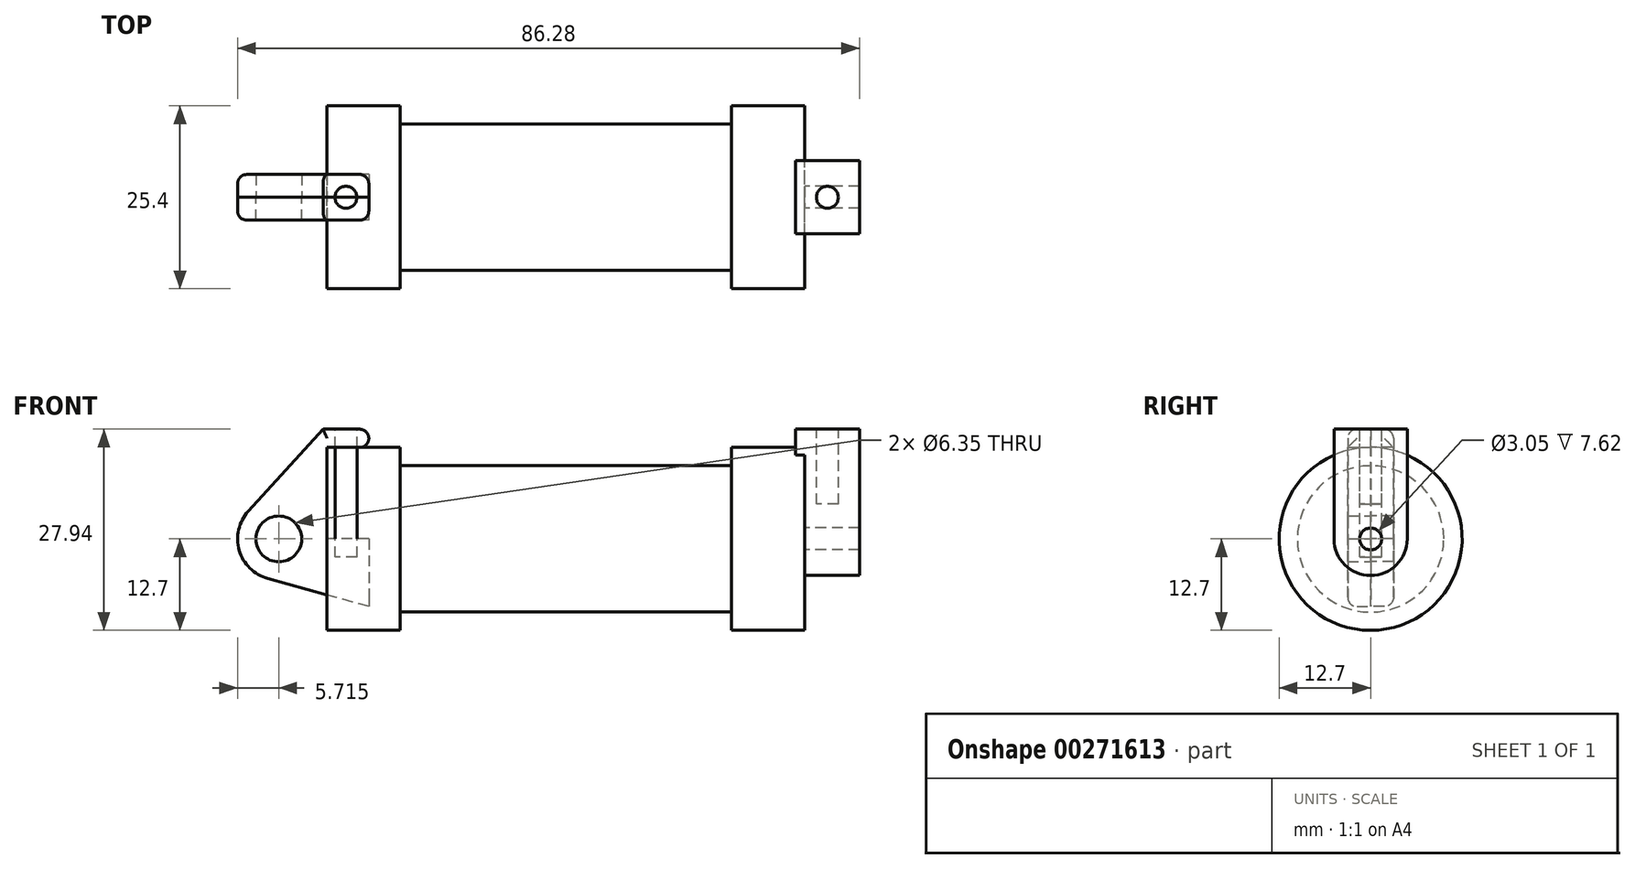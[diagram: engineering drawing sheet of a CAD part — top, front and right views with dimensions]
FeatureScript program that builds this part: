
annotation { "Feature Type Name" : "Feature", "Feature Type Description" : "" }
export const myFeature = defineFeature(function(context is Context, id is Id, definition is map)
    precondition{}
    {
        {
            var Q0;
            Q0=qCreatedBy(makeId("Front.planeOp"),FACE);
            var sketch = newSketch(context, id + "F0", { "sketchPlane" : qUnion([Q0])});
            skLineSegment(sketch, "E0", {"start": v(0, 0) * mm, "end": v(0, 12.7) * mm});
            skLineSegment(sketch, "E1", {"start": v(0, 12.7) * mm, "end": v(10.16, 12.7) * mm});
            skLineSegment(sketch, "E2", {"start": v(10.16, 12.7) * mm, "end": v(10.16, 10.16) * mm});
            skLineSegment(sketch, "E3", {"start": v(10.16, 10.16) * mm, "end": v(56.13, 10.16) * mm});
            skLineSegment(sketch, "E4", {"start": v(56.13, 10.16) * mm, "end": v(56.13, 12.7) * mm});
            skLineSegment(sketch, "E5", {"start": v(56.13, 12.7) * mm, "end": v(66.3, 12.7) * mm});
            skLineSegment(sketch, "E6", {"start": v(66.3, 12.7) * mm, "end": v(66.3, 0) * mm});
            skLineSegment(sketch, "E7", {"start": v(66.3, 0) * mm, "end": v(0, 0) * mm});
            skLineSegment(sketch, "E8", {"start": v(5.84, 15.24) * mm, "end": v(-0.5, 15.24) * mm});
            skLineSegment(sketch, "E9", {"start": v(-0.5, 15.24) * mm, "end": v(-10.88, 3.85) * mm});
            skLineSegment(sketch, "E10", {"start": v(0, 0) * mm, "end": v(-6.65, 0) * mm});
            skCircle(sketch, "E11", {"center": v(-6.65, 0) * mm, "radius": 5.72 * mm});
            skCircle(sketch, "E12", {"center": v(-6.65, 0) * mm, "radius": 3.18 * mm});
            skLineSegment(sketch, "E13", {"start": v(5.84, 15.24) * mm, "end": v(5.84, -9.4) * mm});
            skLineSegment(sketch, "E14", {"start": v(5.84, -9.4) * mm, "end": v(-8.18, -5.5) * mm});
            skSolve(sketch);
        }
        {
            var Q0;
            {var subQ0=sQuery(id+"F0.wireOp",EDGE,"E2");Q0=makeQuery(id+"F0.imprint","IMPRINT",FACE,{"disambiguationData":[TD([[makeQuery(id+"F0.imprint","IMPRINT",EDGE,{"derivedFrom":subQ0}),-1.0]])]});}
            var Q1;
            {var subQ0=sQuery(id+"F0.wireOp",EDGE,"E0");Q1=makeQuery(id+"F0.imprint","IMPRINT",FACE,{"disambiguationData":[TD([[makeQuery(id+"F0.imprint","IMPRINT",EDGE,{"derivedFrom":subQ0}),-1.0]])]});}
            var Q2;
            Q2=sQuery(id+"F0.wireOp",EDGE,"E7");
            revolve(context, id + "F1", {"entities" : qUnion([Q0, Q1]), "axis" : qUnion([Q2]), "revolveType" : RevolveType.FULL});
        }
        {
            var Q0;
            {var subQ3=sQuery(id+"F0.wireOp",EDGE,"E0");Q0=makeQuery(id+"F0.imprint","IMPRINT",FACE,{"disambiguationData":[TD([[makeQuery(id+"F0.imprint","IMPRINT",EDGE,{"derivedFrom":subQ3}),1.0]])]});}
            var Q1;
            {var subQ0=sQuery(id+"F0.wireOp",EDGE,"E14");Q1=makeQuery(id+"F0.imprint","IMPRINT",FACE,{"disambiguationData":[TD([[makeQuery(id+"F0.imprint","IMPRINT",EDGE,{"derivedFrom":subQ0}),-1.0]])]});}
            var Q2;
            {var subQ4=sQuery(id+"F0.wireOp",EDGE,"E12");Q2=makeQuery(id+"F0.imprint","IMPRINT",FACE,{"disambiguationData":[TD([[makeQuery(id+"F0.imprint","IMPRINT",EDGE,{"derivedFrom":subQ4}),-1.0]])]});}
            extrude(context, id + "F2", {"entities" : qUnion([Q0, Q1, Q2]), "depth" : 3.17 * mm});
        }
        {
            var Q0;
            {var subQ3=sQuery(id+"F0.wireOp",EDGE,"E0");Q0=makeQuery(id+"F0.imprint","IMPRINT",FACE,{"disambiguationData":[TD([[makeQuery(id+"F0.imprint","IMPRINT",EDGE,{"derivedFrom":subQ3}),1.0]])]});}
            var Q1;
            {var subQ0=sQuery(id+"F0.wireOp",EDGE,"E14");Q1=makeQuery(id+"F0.imprint","IMPRINT",FACE,{"disambiguationData":[TD([[makeQuery(id+"F0.imprint","IMPRINT",EDGE,{"derivedFrom":subQ0}),-1.0]])]});}
            var Q2;
            {var subQ4=sQuery(id+"F0.wireOp",EDGE,"E12");Q2=makeQuery(id+"F0.imprint","IMPRINT",FACE,{"disambiguationData":[TD([[makeQuery(id+"F0.imprint","IMPRINT",EDGE,{"derivedFrom":subQ4}),-1.0]])]});}
            extrude(context, id + "F3", {"entities" : qUnion([Q0, Q1, Q2]), "oppositeDirection" : true, "depth" : 3.17 * mm});
        }
        {
            var Q0;
            Q0=makeQuery(id+"F1.opRevolve","SWEPT_FACE",FACE,{"disambiguationData":[OSD([sQuery(id+"F0.wireOp",EDGE,"E6")])]});
            var sketch = newSketch(context, id + "F4", { "sketchPlane" : qUnion([Q0])});
            skCircle(sketch, "E15", {"center": v(0, 0) * mm, "radius": 1.52 * mm});
            skCircle(sketch, "E16", {"center": v(0, 0) * mm, "radius": 5.08 * mm});
            skLineSegment(sketch, "E17", {"start": v(-5.08, 0) * mm, "end": v(-5.08, 15.24) * mm});
            skLineSegment(sketch, "E18", {"start": v(5.08, 0) * mm, "end": v(5.08, 15.24) * mm});
            skLineSegment(sketch, "E19", {"start": v(-5.08, 15.24) * mm, "end": v(5.08, 15.24) * mm});
            skSolve(sketch);
        }
        {
            var Q0;
            Q0=makeQuery(id+"F4.imprint","IMPRINT",FACE,{"disambiguationData":[TD([[makeQuery(id+"F4.imprint","IMPRINT",EDGE,{"derivedFrom":sQuery(id+"F4.wireOp",EDGE,"E15")}),-1.0]])]});
            var Q1;
            {var subQ0=sQuery(id+"F4.wireOp",EDGE,"E17");var subQ1=sQuery(id+"F4.wireOp",EDGE,"E16");var subQ2=makeQuery(id+"F4.imprint","INTERSECT",VERTEX,{"derivedFrom":[subQ1,subQ0]});Q1=makeQuery(id+"F4.imprint","IMPRINT",FACE,{"disambiguationData":[TD([[makeQuery(id+"F4.imprint","IMPRINT",EDGE,{"disambiguationData":[TD([[subQ2,1.0]])],"derivedFrom":subQ1}),-1.0]])]});}
            var Q2;
            {var subQ0=sQuery(id+"F4.wireOp",EDGE,"E19");Q2=makeQuery(id+"F4.imprint","IMPRINT",FACE,{"disambiguationData":[TD([[makeQuery(id+"F4.imprint","IMPRINT",EDGE,{"derivedFrom":subQ0}),-1.0]])]});}
            extrude(context, id + "F5", {"entities" : qUnion([Q0, Q1, Q2]), "operationType" : NewBodyOperationType.ADD, "depth" : 7.62 * mm});
        }
        {
            var Q0;
            Q0=makeQuery(id+"F5.opExtrude","CAP_FACE",FACE,{"disambiguationData":[OSD([sQuery(id+"F4.wireOp",EDGE,"E15"),sQuery(id+"F4.wireOp",EDGE,"E16"),sQuery(id+"F4.wireOp",EDGE,"E17"),sQuery(id+"F4.wireOp",EDGE,"E18"),sQuery(id+"F4.wireOp",EDGE,"E19")])],"isStart":true});
            extrude(context, id + "F6", {"entities" : qUnion([Q0]), "operationType" : NewBodyOperationType.ADD, "depth" : 1.27 * mm});
        }
        {
            var Q0;
            Q0=makeQuery(id+"F2.opExtrude","SWEPT_FACE",FACE,{"disambiguationData":[OSD([sQuery(id+"F0.wireOp",EDGE,"E8")])]});
            var sketch = newSketch(context, id + "F7", { "sketchPlane" : qUnion([Q0])});
            skCircle(sketch, "E20", {"center": v(2.67, 0) * mm, "radius": 1.52 * mm});
            skSolve(sketch);
        }
        {
            var Q0;
            {var subQ0=sQuery(id+"F7.wireOp",EDGE,"E20");var subQ1=makeQuery(id+"F2.opExtrude","CAP_EDGE",EDGE,{"disambiguationData":[OSD([sQuery(id+"F0.wireOp",EDGE,"E8")])],"isStart":true});var subQ2=makeQuery(id+"F7.imprint","INTERSECT",VERTEX,{"disambiguationData":[OD(0.0)],"derivedFrom":[subQ1,subQ0]});Q0=makeQuery(id+"F7.imprint","IMPRINT",FACE,{"disambiguationData":[TD([[makeQuery(id+"F7.imprint","IMPRINT",EDGE,{"disambiguationData":[TD([[subQ2,-1.0]])],"derivedFrom":subQ0}),1.0]])]});}
            var Q1;
            {var subQ0=sQuery(id+"F7.wireOp",EDGE,"E20");var subQ1=makeQuery(id+"F2.opExtrude","CAP_EDGE",EDGE,{"disambiguationData":[OSD([sQuery(id+"F0.wireOp",EDGE,"E8")])],"isStart":true});var subQ2=makeQuery(id+"F7.imprint","INTERSECT",VERTEX,{"disambiguationData":[OD(0.0)],"derivedFrom":[subQ1,subQ0]});Q1=makeQuery(id+"F7.imprint","IMPRINT",FACE,{"disambiguationData":[TD([[makeQuery(id+"F7.imprint","IMPRINT",EDGE,{"disambiguationData":[TD([[subQ2,1.0]])],"derivedFrom":subQ0}),1.0]])]});}
            extrude(context, id + "F8", {"entities" : qUnion([Q0, Q1]), "oppositeDirection" : true, "depth" : 17.78 * mm});
        }
        {
            var Q0;
            {var subQ0=sQuery(id+"F4.wireOp",EDGE,"E19");Q0=makeQuery(id+"F6.boolean.opBoolean","MERGE",FACE,{"derivedFrom":[makeQuery(id+"F5.opExtrude","SWEPT_FACE",FACE,{"disambiguationData":[OSD([subQ0])]}),makeQuery(id+"F6.opExtrude","SWEPT_FACE",FACE,{"disambiguationData":[OSD([subQ0])]})]});}
            var sketch = newSketch(context, id + "F9", { "sketchPlane" : qUnion([Q0])});
            skCircle(sketch, "E21", {"center": v(69.47, 0) * mm, "radius": 1.52 * mm});
            skSolve(sketch);
        }
        {
            var Q0;
            Q0 = qSketchRegion(id + "F9", true);
            extrude(context, id + "F10", {"entities" : qUnion([Q0]), "oppositeDirection" : true, "depth" : 10.4 * mm});
        }
        {
            var Q0;
            Q0=makeQuery(id+"F1.opRevolve","SWEPT_EDGE",EDGE,{"disambiguationData":[OSD([sQuery(id+"F0.wireOp",EDGE,"E1"),sQuery(id+"F0.wireOp",EDGE,"E2")])]});
            var Q1;
            Q1=makeQuery(id+"F1.opRevolve","SWEPT_EDGE",EDGE,{"disambiguationData":[OSD([sQuery(id+"F0.wireOp",EDGE,"E2"),sQuery(id+"F0.wireOp",EDGE,"E3")])]});
            var Q2;
            Q2=makeQuery(id+"F1.opRevolve","SWEPT_EDGE",EDGE,{"disambiguationData":[OSD([sQuery(id+"F0.wireOp",EDGE,"E4"),sQuery(id+"F0.wireOp",EDGE,"E5")])]});
            var Q3;
            Q3=makeQuery(id+"F5.boolean.opBoolean","SPLIT",EDGE,{"disambiguationData":[OD(1.0)],"derivedFrom":makeQuery(id+"F1.opRevolve","SWEPT_EDGE",EDGE,{"disambiguationData":[OSD([sQuery(id+"F0.wireOp",EDGE,"E5"),sQuery(id+"F0.wireOp",EDGE,"E6")])]})});
            var Q4;
            Q4=makeQuery(id+"F1.opRevolve","SWEPT_EDGE",EDGE,{"disambiguationData":[OSD([sQuery(id+"F0.wireOp",EDGE,"E0"),sQuery(id+"F0.wireOp",EDGE,"E1")])]});
            var Q5;
            Q5=makeQuery(id+"F1.opRevolve","SWEPT_EDGE",EDGE,{"disambiguationData":[OSD([sQuery(id+"F0.wireOp",EDGE,"E3"),sQuery(id+"F0.wireOp",EDGE,"E4")])]});
            var Q6;
            {var subQ0=sQuery(id+"F0.wireOp",EDGE,"E13");Q6=makeQuery(id+"F2.opExtrude","CAP_EDGE",EDGE,{"disambiguationData":[OSD([subQ0]),TDD([makeQuery(id+"F0.imprint","IMPRINT",EDGE,{"disambiguationData":[TD([[makeQuery(id+"F0.imprint","INTERSECT",VERTEX,{"derivedFrom":[sQuery(id+"F0.wireOp",EDGE,"E8"),subQ0]}),-1.0]])],"derivedFrom":subQ0})])],"isStart":false});}
            var Q7;
            Q7=makeQuery(id+"F2.opExtrude","SWEPT_EDGE",EDGE,{"disambiguationData":[OSD([sQuery(id+"F0.wireOp",EDGE,"E1"),sQuery(id+"F0.wireOp",EDGE,"E13")])]});
            var Q8;
            Q8=makeQuery(id+"F3.opExtrude","SWEPT_EDGE",EDGE,{"disambiguationData":[OSD([sQuery(id+"F0.wireOp",EDGE,"E1"),sQuery(id+"F0.wireOp",EDGE,"E13")])]});
            var Q9;
            Q9=makeQuery(id+"F2.opExtrude","CAP_EDGE",EDGE,{"disambiguationData":[OSD([sQuery(id+"F0.wireOp",EDGE,"E8")])],"isStart":false});
            var Q10;
            Q10=makeQuery(id+"F3.opExtrude","CAP_EDGE",EDGE,{"disambiguationData":[OSD([sQuery(id+"F0.wireOp",EDGE,"E8")])],"isStart":false});
            var Q11;
            {var subQ0=sQuery(id+"F4.wireOp",EDGE,"E19");var subQ1=sQuery(id+"F4.wireOp",EDGE,"E17");Q11=makeQuery(id+"F6.boolean.opBoolean","MERGE",EDGE,{"derivedFrom":[makeQuery(id+"F5.opExtrude","SWEPT_EDGE",EDGE,{"disambiguationData":[OSD([subQ1,subQ0])]}),makeQuery(id+"F6.opExtrude","SWEPT_EDGE",EDGE,{"disambiguationData":[OSD([subQ1,subQ0])]})]});}
            var Q12;
            {var subQ0=sQuery(id+"F4.wireOp",EDGE,"E19");Q12=makeQuery(id+"F6.boolean.opBoolean","MERGE",FACE,{"derivedFrom":[makeQuery(id+"F5.opExtrude","SWEPT_FACE",FACE,{"disambiguationData":[OSD([subQ0])]}),makeQuery(id+"F6.opExtrude","SWEPT_FACE",FACE,{"disambiguationData":[OSD([subQ0])]})]});}
            var Q13;
            Q13=makeQuery(id+"F5.opExtrude","CAP_FACE",FACE,{"disambiguationData":[OSD([sQuery(id+"F4.wireOp",EDGE,"E15"),sQuery(id+"F4.wireOp",EDGE,"E16"),sQuery(id+"F4.wireOp",EDGE,"E17"),sQuery(id+"F4.wireOp",EDGE,"E18"),sQuery(id+"F4.wireOp",EDGE,"E19")])],"isStart":false});
            var Q14;
            Q14=makeQuery(id+"F2.opExtrude","CAP_EDGE",EDGE,{"disambiguationData":[OSD([sQuery(id+"F0.wireOp",EDGE,"E14")])],"isStart":false});
            var Q15;
            Q15=makeQuery(id+"F3.opExtrude","CAP_EDGE",EDGE,{"disambiguationData":[OSD([sQuery(id+"F0.wireOp",EDGE,"E14")])],"isStart":false});
            var Q16;
            {var subQ0=sQuery(id+"F4.wireOp",EDGE,"E17");var subQ1=sQuery(id+"F4.wireOp",EDGE,"E16");Q16=makeQuery(id+"F5.boolean.opBoolean","SPLIT",EDGE,{"disambiguationData":[TD([makeQuery(id+"F5.opExtrude","SWEPT_FACE",FACE,{"disambiguationData":[OSD([subQ1])]})])],"derivedFrom":makeQuery(id+"F5.opExtrude","CAP_EDGE",EDGE,{"disambiguationData":[OSD([subQ0])],"isStart":true})});}
            var Q17;
            Q17=makeQuery(id+"F5.opExtrude","CAP_EDGE",EDGE,{"disambiguationData":[OSD([sQuery(id+"F4.wireOp",EDGE,"E16")])],"isStart":true});
            var Q18;
            Q18=makeQuery(id+"F5.boolean.opBoolean","SPLIT",FACE,{"disambiguationData":[TD([makeQuery(id+"F1.opRevolve","SWEPT_FACE",FACE,{"disambiguationData":[OSD([sQuery(id+"F0.wireOp",EDGE,"E5")])]})])],"derivedFrom":makeQuery(id+"F1.opRevolve","SWEPT_FACE",FACE,{"disambiguationData":[OSD([sQuery(id+"F0.wireOp",EDGE,"E6")])]})});
            var Q19;
            Q19=makeQuery(id+"F3.opExtrude","SWEPT_EDGE",EDGE,{"disambiguationData":[OSD([sQuery(id+"F0.wireOp",EDGE,"E8"),sQuery(id+"F0.wireOp",EDGE,"E13")])]});
            var Q20;
            Q20=makeQuery(id+"F2.opExtrude","SWEPT_EDGE",EDGE,{"disambiguationData":[OSD([sQuery(id+"F0.wireOp",EDGE,"E8"),sQuery(id+"F0.wireOp",EDGE,"E13")])]});
            var Q21;
            {var subQ0=sQuery(id+"F0.wireOp",EDGE,"E13");Q21=makeQuery(id+"F3.opExtrude","CAP_EDGE",EDGE,{"disambiguationData":[OSD([subQ0]),TDD([makeQuery(id+"F0.imprint","IMPRINT",EDGE,{"disambiguationData":[TD([[makeQuery(id+"F0.imprint","INTERSECT",VERTEX,{"derivedFrom":[sQuery(id+"F0.wireOp",EDGE,"E8"),subQ0]}),-1.0]])],"derivedFrom":subQ0})])],"isStart":false});}
            fillet(context, id + "F11", {"entities" : qUnion([Q0, Q1, Q2, Q3, Q4, Q5, Q6, Q7, Q8, Q9, Q10, Q11, Q12, Q13, Q14, Q15, Q16, Q17, Q18, Q19, Q20, Q21]), "radius" : 1.27 * mm, "tangentPropagation" : true, "allowEdgeOverflow" : false});
        }
    });
